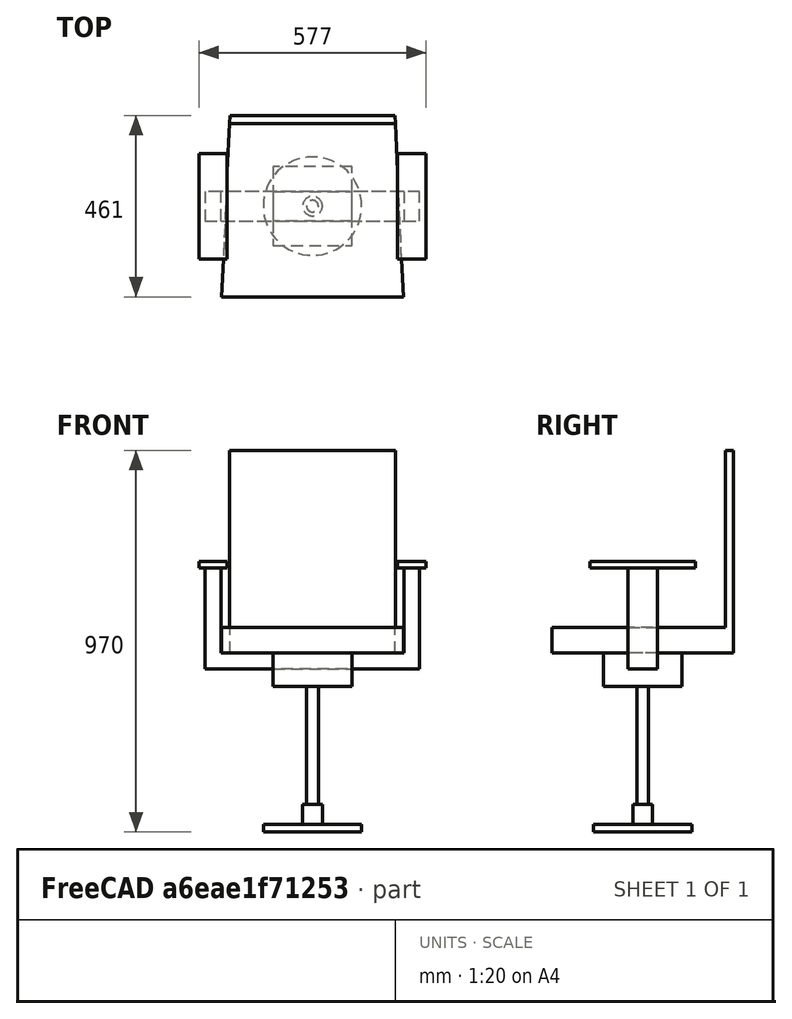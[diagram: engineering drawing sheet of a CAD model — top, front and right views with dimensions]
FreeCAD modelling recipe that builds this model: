
FCSTD DOCUMENT  (FreeCAD 1.0R39109 (Git))
Label: chair02_00502
License: All rights reserved
LicenseURL: https://en.wikipedia.org/wiki/All_rights_reserved
objects: Sketcher::SketchObject×10, PartDesign::Pad×10, TechDraw::DrawViewDimension×9, TechDraw::DrawViewAnnotation×9, PartDesign::Body×5, PartDesign::ShapeBinder×4, TechDraw::DrawSVGTemplate×3, TechDraw::DrawProjGroupItem×3, TechDraw::DrawPage×3, TechDraw::DrawViewSection×3, App::Part×1
note: 76 computed .brp shape members not serialized (recipe doc carries the construction recipe); baked Part::Feature solids carry a one-line shape summary decoded from their .brp

FEATURE [Sketcher::SketchObject] Sketch
  ArcFitTolerance = 1e-06
  AttachmentSupport = -> [XY_Plane]
  FullyConstrained = true
  MakeInternals = false
  MapMode = 5
  sketch-geometry (1):
    g0: Circle CenterX=0 CenterY=0 CenterZ=0 NormalX=0 NormalY=0 NormalZ=1 AngleXU=0 Radius=125
  constraints (2):
    c: Diameter(g0) = 250
    c: Coincident(g0,g-1)
FEATURE [PartDesign::Pad] Pad
  Direction = (0,0,1)
  Length = 20
  Length2 = 10
  Profile = -> Sketch
  ReferenceAxis = -> Sketch [N_Axis]
  Refine = true
  Suppressed = false
  Type = 0
FEATURE [Sketcher::SketchObject] Sketch001
  ArcFitTolerance = 1e-06
  AttachmentSupport = -> [Pad]
  FullyConstrained = true
  MakeInternals = false
  MapMode = 5
  Placement = pos=(0,0,20) rot=(0,0,1;0rad)
  sketch-geometry (1):
    g0: Circle CenterX=0 CenterY=0 CenterZ=0 NormalX=0 NormalY=0 NormalZ=1 AngleXU=0 Radius=25
  constraints (2):
    c: Diameter(g0) = 50
    c: Coincident(g0,g-1)
FEATURE [PartDesign::Pad] Pad001
  BaseFeature = -> Pad
  Direction = (0,0,1)
  Length = 50
  Length2 = 10
  Profile = -> Sketch001
  ReferenceAxis = -> Sketch001 [N_Axis]
  Refine = true
  Suppressed = false
  Type = 0
FEATURE [PartDesign::Body] Body  label="Body1"
  AllowCompound = false
  Group = -> [Sketch,Pad,Sketch001,Pad001]
  Origin = -> Origin
  Tip = -> Pad001
FEATURE [PartDesign::ShapeBinder] CopyPad001  label="Body2_Sketch_P.lane"
  Placement = pos=(0,0,50) rot=(0,0,1;0rad)
  TraceSupport = false
FEATURE [Sketcher::SketchObject] Sketch002
  ArcFitTolerance = 1e-06
  AttachmentSupport = -> [CopyPad001]
  FullyConstrained = true
  MakeInternals = false
  MapMode = 5
  Placement = pos=(0,0,70) rot=(0,0,1;0rad)
  sketch-geometry (1):
    g0: Circle CenterX=0 CenterY=0 CenterZ=0 NormalX=0 NormalY=0 NormalZ=1 AngleXU=0 Radius=15
  constraints (2):
    c: Diameter(g0) = 30
    c: Coincident(g0,g-1)
FEATURE [PartDesign::Pad] Pad002
  Direction = (0,0,1)
  Length = 300
  Length2 = 10
  Placement = pos=(0,0,50) rot=(0,0,1;0rad)
  Profile = -> Sketch002
  ReferenceAxis = -> Sketch002 [N_Axis]
  Refine = true
  Suppressed = false
  Type = 0
FEATURE [PartDesign::Body] Body001  label="Body2"
  AllowCompound = false
  Group = -> [CopyPad001,Sketch002,Pad002]
  Origin = -> Origin001
  Tip = -> Pad002
FEATURE [PartDesign::ShapeBinder] CopyPad002  label="Body3_Sketch_Plane"
  Placement = pos=(0,0,300) rot=(0,0,1;0rad)
  TraceSupport = false
FEATURE [Sketcher::SketchObject] Sketch003
  ArcFitTolerance = 1e-06
  AttachmentSupport = -> [CopyPad002]
  FullyConstrained = true
  MakeInternals = false
  MapMode = 5
  Placement = pos=(0,0,370) rot=(0,0,1;0rad)
  sketch-geometry (5):
    g0: LineSegment StartX=-100 StartY=-100 StartZ=0 EndX=100 EndY=-100 EndZ=0
    g1: LineSegment StartX=100 StartY=-100 StartZ=0 EndX=100 EndY=100 EndZ=0
    g2: LineSegment StartX=100 StartY=100 StartZ=0 EndX=-100 EndY=100 EndZ=0
    g3: LineSegment StartX=-100 StartY=100 StartZ=0 EndX=-100 EndY=-100 EndZ=0
    g4: GeomPoint [constr] X=0 Y=0 Z=0
  constraints (12):
    c: Coincident(g0,g1)
    c: Coincident(g1,g2)
    c: Coincident(g2,g3)
    c: Coincident(g3,g0)
    c: Horizontal(g0)
    c: Horizontal(g2)
    c: Vertical(g1)
    c: Vertical(g3)
    c: Symmetric(g2,g0,g4)
    c: Distance(g1,g3) = 200
    c: Distance(g0,g2) = 200
    c: Coincident(g4,g-1)
FEATURE [PartDesign::Pad] Pad003
  Direction = (0,0,1)
  Length = 45
  Length2 = 10
  Placement = pos=(0,0,300) rot=(0,0,1;0rad)
  Profile = -> Sketch003
  ReferenceAxis = -> Sketch003 [N_Axis]
  Refine = true
  Suppressed = false
  Type = 0
FEATURE [PartDesign::ShapeBinder] CopyPad003  label="Body4_Sketch_Plane"
  Placement = pos=(0,0,45) rot=(0,0,1;0rad)
  TraceSupport = false
FEATURE [Sketcher::SketchObject] Sketch004
  ArcFitTolerance = 1e-06
  AttachmentSupport = -> [CopyPad003]
  FullyConstrained = true
  MakeInternals = false
  MapMode = 5
  Placement = pos=(0,0,415) rot=(0,0,1;0rad)
  sketch-geometry (5):
    g0: LineSegment StartX=-272.5 StartY=-37.5 StartZ=0 EndX=272.5 EndY=-37.5 EndZ=0
    g1: LineSegment StartX=272.5 StartY=-37.5 StartZ=0 EndX=272.5 EndY=37.5 EndZ=0
    g2: LineSegment StartX=272.5 StartY=37.5 StartZ=0 EndX=-272.5 EndY=37.5 EndZ=0
    g3: LineSegment StartX=-272.5 StartY=37.5 StartZ=0 EndX=-272.5 EndY=-37.5 EndZ=0
    g4: GeomPoint [constr] X=0 Y=0 Z=0
  constraints (12):
    c: Coincident(g0,g1)
    c: Coincident(g1,g2)
    c: Coincident(g2,g3)
    c: Coincident(g3,g0)
    c: Horizontal(g0)
    c: Horizontal(g2)
    c: Vertical(g1)
    c: Vertical(g3)
    c: Symmetric(g2,g0,g4)
    c: Distance(g1,g3) = 545
    c: Distance(g0,g2) = 75
    c: Coincident(g4,g-1)
FEATURE [PartDesign::Pad] Pad004
  Direction = (0,0,1)
  Length = 40
  Length2 = 10
  Placement = pos=(0,0,45) rot=(0,0,1;0rad)
  Profile = -> Sketch004
  ReferenceAxis = -> Sketch004 [N_Axis]
  Refine = true
  Suppressed = false
  Type = 0
FEATURE [Sketcher::SketchObject] Sketch005
  ArcFitTolerance = 1e-06
  AttachmentSupport = -> [Pad004]
  ExternalGeometry = -> [Pad004]
  FullyConstrained = true
  MakeInternals = false
  MapMode = 5
  Placement = pos=(0,0,455) rot=(0,0,1;0rad)
  sketch-geometry (8):
    g0: LineSegment StartX=-272.5 StartY=37.5 StartZ=0 EndX=-272.5 EndY=-37.5 EndZ=0
    g1: LineSegment StartX=-272.5 StartY=-37.5 StartZ=0 EndX=-232.5 EndY=-37.5 EndZ=0
    g2: LineSegment StartX=-232.5 StartY=-37.5 StartZ=0 EndX=-232.5 EndY=37.5 EndZ=0
    g3: LineSegment StartX=-232.5 StartY=37.5 StartZ=0 EndX=-272.5 EndY=37.5 EndZ=0
    g4: LineSegment StartX=272.5 StartY=37.5 StartZ=0 EndX=232.5 EndY=37.5 EndZ=0
    g5: LineSegment StartX=232.5 StartY=37.5 StartZ=0 EndX=232.5 EndY=-37.5 EndZ=0
    g6: LineSegment StartX=232.5 StartY=-37.5 StartZ=0 EndX=272.5 EndY=-37.5 EndZ=0
    g7: LineSegment StartX=272.5 StartY=-37.5 StartZ=0 EndX=272.5 EndY=37.5 EndZ=0
  constraints (22):
    c: Coincident(g0,g1)
    c: Coincident(g1,g2)
    c: Coincident(g2,g3)
    c: Coincident(g3,g0)
    c: Vertical(g0)
    c: Vertical(g2)
    c: Horizontal(g1)
    c: Horizontal(g3)
    c: Coincident(g0,g-3)
    c: PointOnObject(g1,g-4)
    c: DistanceX(g3,g3) = 40
    c: Coincident(g4,g5)
    c: Coincident(g5,g6)
    c: Coincident(g6,g7)
    c: Coincident(g7,g4)
    c: Horizontal(g4)
    c: Horizontal(g6)
    c: Vertical(g5)
    c: Vertical(g7)
    c: Coincident(g4,g-3)
    c: PointOnObject(g5,g-4)
    c: Equal(g4,g3)
FEATURE [PartDesign::Pad] Pad005
  BaseFeature = -> Pad004
  Direction = (0,0,1)
  Length = 216
  Length2 = 10
  Placement = pos=(0,0,45) rot=(0,0,1;0rad)
  Profile = -> Sketch005
  ReferenceAxis = -> Sketch005 [N_Axis]
  Refine = true
  Suppressed = false
  Type = 0
FEATURE [Sketcher::SketchObject] Sketch006
  ArcFitTolerance = 1e-06
  AttachmentSupport = -> [Pad005]
  ExternalGeometry = -> [Pad005]
  FullyConstrained = true
  MakeInternals = false
  MapMode = 5
  Placement = pos=(0,0,671) rot=(0,0,1;0rad)
  sketch-geometry (16):
    g0: LineSegment StartX=-288.5 StartY=134 StartZ=0 EndX=-288.5 EndY=-134 EndZ=0
    g1: LineSegment StartX=-288.5 StartY=-134 StartZ=0 EndX=-216.5 EndY=-134 EndZ=0
    g2: LineSegment StartX=-216.5 StartY=-134 StartZ=0 EndX=-216.5 EndY=134 EndZ=0
    g3: LineSegment StartX=-216.5 StartY=134 StartZ=0 EndX=-288.5 EndY=134 EndZ=0
    g4: LineSegment StartX=216.5 StartY=134 StartZ=0 EndX=216.5 EndY=-134 EndZ=0
    g5: LineSegment StartX=216.5 StartY=-134 StartZ=0 EndX=288.5 EndY=-134 EndZ=0
    g6: LineSegment StartX=288.5 StartY=-134 StartZ=0 EndX=288.5 EndY=134 EndZ=0
    g7: LineSegment StartX=288.5 StartY=134 StartZ=0 EndX=216.5 EndY=134 EndZ=0
    g8: LineSegment [constr] StartX=-272.5 StartY=37.5 StartZ=0 EndX=-232.5 EndY=-37.5 EndZ=0
    g9: LineSegment [constr] StartX=-252.5 StartY=0 StartZ=0 EndX=-272.5 EndY=-37.5 EndZ=0
    g10: LineSegment [constr] StartX=232.5 StartY=37.5 StartZ=0 EndX=272.5 EndY=-37.5 EndZ=0
    g11: LineSegment [constr] StartX=272.5 StartY=37.5 StartZ=0 EndX=252.5 EndY=0 EndZ=0
    g12: LineSegment [constr] StartX=-216.5 StartY=134 StartZ=0 EndX=-288.5 EndY=-134 EndZ=0
    g13: LineSegment [constr] StartX=-288.5 StartY=134 StartZ=0 EndX=-252.5 EndY=0 EndZ=0
    g14: LineSegment [constr] StartX=216.5 StartY=134 StartZ=0 EndX=288.5 EndY=-134 EndZ=0
    g15: LineSegment [constr] StartX=288.5 StartY=134 StartZ=0 EndX=252.5 EndY=0 EndZ=0
  constraints (38):
    c: Coincident(g0,g1)
    c: Coincident(g1,g2)
    c: Coincident(g2,g3)
    c: Coincident(g3,g0)
    c: Vertical(g0)
    c: Vertical(g2)
    c: Horizontal(g1)
    c: Horizontal(g3)
    c: Coincident(g4,g5)
    c: Coincident(g5,g6)
    c: Coincident(g6,g7)
    c: Coincident(g7,g4)
    c: Vertical(g4)
    c: Vertical(g6)
    c: Horizontal(g5)
    c: Horizontal(g7)
    c: Equal(g7,g3)
    c: Equal(g2,g4)
    c: DistanceX(g3,g3) = 72
    c: Coincident(g8,g-4)
    c: Coincident(g8,g-3)
    c: Coincident(g9,g-4)
    c: Coincident(g10,g-5)
    c: Coincident(g10,g-6)
    c: Coincident(g11,g-6)
    c: Symmetric(g10,g10,g11)
    c: Symmetric(g8,g8,g9)
    c: Coincident(g12,g2)
    c: Coincident(g12,g0)
    c: Coincident(g13,g0)
    c: Symmetric(g12,g12,g13)
    c: Coincident(g9,g13)
    c: Coincident(g14,g4)
    c: Coincident(g14,g5)
    c: Coincident(g15,g6)
    c: Symmetric(g14,g14,g15)
    c: Coincident(g15,g11)
    c: DistanceY(g2,g2) = 268
FEATURE [PartDesign::Pad] Pad006
  BaseFeature = -> Pad005
  Direction = (0,0,1)
  Length = 17
  Length2 = 10
  Placement = pos=(0,0,45) rot=(0,0,1;0rad)
  Profile = -> Sketch006
  ReferenceAxis = -> Sketch006 [N_Axis]
  Refine = true
  Suppressed = false
  Type = 0
FEATURE [PartDesign::Body] Body003  label="Body4"
  AllowCompound = false
  Group = -> [CopyPad003,Sketch004,Pad004,Sketch005,Pad005,Sketch006,Pad006]
  Origin = -> Origin003
  Tip = -> Pad006
FEATURE [PartDesign::ShapeBinder] CopyPad006  label="Body5_Sketch_Plane"
  Placement = pos=(0,0,45) rot=(0,0,1;0rad)
  TraceSupport = false
FEATURE [Sketcher::SketchObject] Sketch009
  ArcFitTolerance = 1e-06
  AttachmentSupport = -> [Pad003]
  ExternalGeometry = -> [Pad003]
  FullyConstrained = true
  MakeInternals = false
  MapMode = 5
  Placement = pos=(0,0,415) rot=(0,0,1;0rad)
  sketch-geometry (8):
    g0: LineSegment StartX=-100 StartY=100 StartZ=0 EndX=-100 EndY=37.5 EndZ=0
    g1: LineSegment StartX=-100 StartY=37.5 StartZ=0 EndX=100 EndY=37.5 EndZ=0
    g2: LineSegment StartX=100 StartY=37.5 StartZ=0 EndX=100 EndY=100 EndZ=0
    g3: LineSegment StartX=100 StartY=100 StartZ=0 EndX=-100 EndY=100 EndZ=0
    g4: LineSegment StartX=100 StartY=-100 StartZ=0 EndX=100 EndY=-37.5 EndZ=0
    g5: LineSegment StartX=100 StartY=-37.5 StartZ=0 EndX=-100 EndY=-37.5 EndZ=0
    g6: LineSegment StartX=-100 StartY=-37.5 StartZ=0 EndX=-100 EndY=-100 EndZ=0
    g7: LineSegment StartX=-100 StartY=-100 StartZ=0 EndX=100 EndY=-100 EndZ=0
  constraints (21):
    c: Coincident(g0,g1)
    c: Coincident(g1,g2)
    c: Coincident(g2,g3)
    c: Coincident(g3,g0)
    c: Vertical(g0)
    c: Vertical(g2)
    c: Horizontal(g1)
    c: Horizontal(g3)
    c: Coincident(g0,g-3)
    c: PointOnObject(g1,g-4)
    c: Coincident(g4,g5)
    c: Coincident(g5,g6)
    c: Coincident(g6,g7)
    c: Coincident(g7,g4)
    c: Vertical(g6)
    c: Horizontal(g5)
    c: Horizontal(g7)
    c: Coincident(g4,g-4)
    c: PointOnObject(g5,g-3)
    c: DistanceY(g4,g1) = 75
    c: Symmetric(g1,g4,g-1)
FEATURE [PartDesign::Pad] Pad009
  BaseFeature = -> Pad003
  Direction = (0,0,1)
  Length = 40
  Length2 = 10
  Placement = pos=(0,0,300) rot=(0,0,1;0rad)
  Profile = -> Sketch009
  ReferenceAxis = -> Sketch009 [N_Axis]
  Refine = true
  Suppressed = false
  Type = 0
FEATURE [PartDesign::Body] Body002  label="Body3"
  AllowCompound = false
  Group = -> [CopyPad002,Sketch003,Pad003,Sketch009,Pad009]
  Origin = -> Origin002
  Tip = -> Pad009
FEATURE [Sketcher::SketchObject] Sketch007
  ArcFitTolerance = 1e-06
  AttachmentSupport = -> [CopyPad006]
  FullyConstrained = true
  MakeInternals = false
  MapMode = 5
  Placement = pos=(0,0,455) rot=(0,0,1;0rad)
  sketch-geometry (8):
    g0: LineSegment StartX=-210 StartY=230.5 StartZ=0 EndX=-231 EndY=-230.5 EndZ=0
    g1: LineSegment StartX=-231 StartY=-230.5 StartZ=0 EndX=231 EndY=-230.5 EndZ=0
    g2: LineSegment StartX=231 StartY=-230.5 StartZ=0 EndX=210 EndY=230.5 EndZ=0
    g3: LineSegment StartX=210 StartY=230.5 StartZ=0 EndX=-210 EndY=230.5 EndZ=0
    g4: LineSegment [constr] StartX=210 StartY=230.5 StartZ=0 EndX=2.84e-14 EndY=0 EndZ=0
    g5: LineSegment [constr] StartX=2.84e-14 StartY=0 StartZ=0 EndX=-210 EndY=230.5 EndZ=0
    g6: LineSegment [constr] StartX=210 StartY=230.5 StartZ=0 EndX=210 EndY=0 EndZ=0
    g7: LineSegment [constr] StartX=231 StartY=-230.5 StartZ=0 EndX=231 EndY=0 EndZ=0
  constraints (20):
    c: Coincident(g2,g1)
    c: DistanceX(g1,g1) = 462
    c: DistanceX(g3,g3) = 420
    c: Coincident(g1,g0)
    c: Symmetric(g2,g0,g-2)
    c: Coincident(g2,g3)
    c: Coincident(g3,g0)
    c: Coincident(g4,g2)
    c: Coincident(g4,g-1)
    c: Coincident(g5,g4)
    c: Coincident(g5,g0)
    c: DistanceY(g2,g2) = 461
    c: Coincident(g6,g2)
    c: PointOnObject(g6,g-1)
    c: Vertical(g6)
    c: Coincident(g7,g1)
    c: PointOnObject(g7,g-1)
    c: Vertical(g7)
    c: Equal(g7,g6)
    c: Symmetric(g1,g0,g-2)
FEATURE [PartDesign::Pad] Pad007
  Direction = (0,0,1)
  Length = 65
  Length2 = 10
  Placement = pos=(0,0,45) rot=(0,0,1;0rad)
  Profile = -> Sketch007
  ReferenceAxis = -> Sketch007 [N_Axis]
  Refine = true
  Suppressed = false
  Type = 0
FEATURE [Sketcher::SketchObject] Sketch008
  ArcFitTolerance = 1e-06
  AttachmentSupport = -> [Pad007]
  ExternalGeometry = -> [Pad007]
  FullyConstrained = true
  MakeInternals = false
  MapMode = 5
  Placement = pos=(0,0,520) rot=(0,0,1;0rad)
  sketch-geometry (4):
    g0: LineSegment StartX=-210 StartY=230.5 StartZ=0 EndX=210 EndY=230.5 EndZ=0
    g1: LineSegment StartX=-210 StartY=230.5 StartZ=0 EndX=-210.957 EndY=209.5 EndZ=0
    g2: LineSegment StartX=-210.957 StartY=209.5 StartZ=0 EndX=210.957 EndY=209.5 EndZ=0
    g3: LineSegment StartX=210 StartY=230.5 StartZ=0 EndX=210.957 EndY=209.5 EndZ=0
  constraints (10):
    c: Coincident(g0,g-3)
    c: Coincident(g0,g-4)
    c: Coincident(g1,g0)
    c: PointOnObject(g1,g-3)
    c: Coincident(g2,g1)
    c: PointOnObject(g2,g-4)
    c: Horizontal(g2)
    c: Coincident(g3,g0)
    c: Coincident(g3,g2)
    c: DistanceY(g1,g1) = 21
FEATURE [PartDesign::Pad] Pad008
  BaseFeature = -> Pad007
  Direction = (0,0,1)
  Length = 450
  Length2 = 10
  Placement = pos=(0,0,45) rot=(0,0,1;0rad)
  Profile = -> Sketch008
  ReferenceAxis = -> Sketch008 [N_Axis]
  Refine = true
  Suppressed = false
  Type = 0
FEATURE [PartDesign::Body] Body004  label="Body5"
  AllowCompound = false
  Group = -> [CopyPad006,Sketch007,Pad007,Sketch008,Pad008]
  Origin = -> Origin004
  Tip = -> Pad008
FEATURE [App::Part] Part  label="chair02"
  Group = -> [Body,Body001,Body002,Body003,Body004]
  Origin = -> Origin005
FEATURE [TechDraw::DrawSVGTemplate] Template  label="テンプレート"
  Height = 210
  Orientation = 1
  Template = <userpath>/AppData/Local/Programs/FreeCAD 1.0/data/Mod/TechDraw/Templates/A4_Landscape_blank.svg
  Width = 297
FEATURE [TechDraw::DrawProjGroupItem] View
  CoarseView = false
  Direction = (0,0,1)
  Focus = 100
  HardHidden = true
  IsoCount = 0
  IsoHidden = false
  IsoVisible = false
  LockPosition = false
  Perspective = false
  Rotation = 0
  RotationVector = (1,0,0)
  Scale = 0.333333
  ScaleType = 2
  ScrubCount = 1
  SeamHidden = false
  SeamVisible = false
  SmoothHidden = false
  SmoothVisible = true
  Source = -> [Part]
  Type = 0
  X = 131.425
  XDirection = (1,0,0)
  Y = 107.897
FEATURE [TechDraw::DrawViewDimension] Dimension  label="寸法"
  AngleOverride = false
  Arbitrary = false
  ArbitraryTolerances = false
  BoxCorners = (2) [(-96.1666,-76.8333,0),(96.1666,76.8333,0)]
  EqualTolerance = true
  ExtensionAngle = 0
  FormatSpec = %.2w
  FormatSpecOverTolerance = %+.2w
  FormatSpecUnderTolerance = %+.2w
  Inverted = false
  LineAngle = 0
  LockPosition = false
  MeasureType = 1
  OverTolerance = 0
  References2D = -> [View]
  Rotation = 0
  Scale = 0.2
  ScaleType = 2
  TheoreticalExact = false
  Type = 1
  UnderTolerance = 0
  X = 0
  Y = 93.9298
FEATURE [TechDraw::DrawViewDimension] Dimension001  label="寸法001"
  AngleOverride = false
  Arbitrary = false
  ArbitraryTolerances = false
  BoxCorners = (2) [(-96.1666,-76.8333,0),(96.1666,76.8333,0)]
  EqualTolerance = true
  ExtensionAngle = 0
  FormatSpec = %.2w
  FormatSpecOverTolerance = %+.2w
  FormatSpecUnderTolerance = %+.2w
  Inverted = false
  LineAngle = 0
  LockPosition = false
  MeasureType = 1
  OverTolerance = 0
  References2D = -> [View]
  Rotation = 0
  Scale = 0.2
  ScaleType = 2
  TheoreticalExact = false
  Type = 2
  UnderTolerance = 0
  X = 135.701
  Y = 0
FEATURE [TechDraw::DrawViewDimension] Dimension002  label="寸法002"
  AngleOverride = false
  Arbitrary = false
  ArbitraryTolerances = false
  BoxCorners = (2) [(-96.1666,-76.8333,0),(96.1666,76.8333,0)]
  EqualTolerance = true
  ExtensionAngle = 0
  FormatSpec = %.2w
  FormatSpecOverTolerance = %+.2w
  FormatSpecUnderTolerance = %+.2w
  Inverted = false
  LineAngle = 0
  LockPosition = false
  MeasureType = 1
  OverTolerance = 0
  References2D = -> [View]
  Rotation = 0
  Scale = 0.2
  ScaleType = 2
  TheoreticalExact = false
  Type = 2
  UnderTolerance = 0
  X = 113.57
  Y = 61.6706
FEATURE [TechDraw::DrawViewDimension] Dimension003  label="寸法003"
  AngleOverride = false
  Arbitrary = false
  ArbitraryTolerances = false
  BoxCorners = (2) [(-96.1666,-76.8333,0),(96.1666,76.8333,0)]
  EqualTolerance = true
  ExtensionAngle = 0
  FormatSpec = %.2w
  FormatSpecOverTolerance = %+.2w
  FormatSpecUnderTolerance = %+.2w
  Inverted = false
  LineAngle = 0
  LockPosition = false
  MeasureType = 1
  OverTolerance = 0
  References2D = -> [View]
  Rotation = 0
  Scale = 0.2
  ScaleType = 2
  TheoreticalExact = false
  Type = 2
  UnderTolerance = 0
  X = 125.233
  Y = 0.063601
FEATURE [TechDraw::DrawViewDimension] Dimension004  label="寸法004"
  AngleOverride = false
  Arbitrary = false
  ArbitraryTolerances = false
  BoxCorners = (2) [(-96.1666,-76.8333,0),(96.1666,76.8333,0)]
  EqualTolerance = true
  ExtensionAngle = 0
  FormatSpec = %.2w
  FormatSpecOverTolerance = %+.2w
  FormatSpecUnderTolerance = %+.2w
  Inverted = false
  LineAngle = 0
  LockPosition = false
  MeasureType = 1
  OverTolerance = 0
  References2D = -> [View]
  Rotation = 0
  Scale = 0.2
  ScaleType = 2
  TheoreticalExact = false
  Type = 1
  UnderTolerance = 0
  X = -84.1666
  Y = 58.5053
FEATURE [TechDraw::DrawViewDimension] Dimension005  label="寸法005"
  AngleOverride = false
  Arbitrary = false
  ArbitraryTolerances = false
  BoxCorners = (2) [(-96.1666,-76.8333,0),(96.1666,76.8333,0)]
  EqualTolerance = true
  ExtensionAngle = 0
  FormatSpec = %.2w
  FormatSpecOverTolerance = %+.2w
  FormatSpecUnderTolerance = %+.2w
  Inverted = false
  LineAngle = 0
  LockPosition = false
  MeasureType = 1
  OverTolerance = 0
  References2D = -> [View]
  Rotation = 0
  Scale = 0.2
  ScaleType = 2
  TheoreticalExact = false
  Type = 2
  UnderTolerance = 0
  X = -108.801
  Y = 0
FEATURE [TechDraw::DrawViewDimension] Dimension006  label="寸法006"
  AngleOverride = false
  Arbitrary = false
  ArbitraryTolerances = false
  BoxCorners = (2) [(-96.1666,-76.8333,0),(96.1666,76.8333,0)]
  EqualTolerance = true
  ExtensionAngle = 0
  FormatSpec = %.2w
  FormatSpecOverTolerance = %+.2w
  FormatSpecUnderTolerance = %+.2w
  Inverted = false
  LineAngle = 0
  LockPosition = false
  MeasureType = 1
  OverTolerance = 0
  References2D = -> [View]
  Rotation = 0
  Scale = 0.2
  ScaleType = 2
  TheoreticalExact = false
  Type = 1
  UnderTolerance = 0
  X = 0
  Y = -83.8244
FEATURE [TechDraw::DrawPage] Page  label="用紙"
  KeepUpdated = true
  NextBalloonIndex = 1
  ProjectionType = 0
  Template = -> Template
  Views = -> [View,Dimension,Dimension001,Dimension002,Dimension003,Dimension004,Dimension005,Dimension006]
FEATURE [TechDraw::DrawSVGTemplate] Template001  label="テンプレート001"
  Height = 210
  Orientation = 1
  Template = <userpath>/AppData/Local/Programs/FreeCAD 1.0/data/Mod/TechDraw/Templates/A4_Landscape_blank.svg
  Width = 297
FEATURE [TechDraw::DrawSVGTemplate] Template002  label="テンプレート002"
  Height = 210
  Orientation = 1
  Template = <userpath>/AppData/Local/Programs/FreeCAD 1.0/data/Mod/TechDraw/Templates/A4_Landscape_blank.svg
  Width = 297
FEATURE [TechDraw::DrawProjGroupItem] View001
  CoarseView = false
  Direction = (0,-1,0)
  Focus = 100
  HardHidden = true
  IsoCount = 0
  IsoHidden = false
  IsoVisible = false
  LockPosition = false
  Perspective = false
  Rotation = 0
  RotationVector = (1,0,0)
  Scale = 0.2
  ScaleType = 2
  ScrubCount = 1
  SeamHidden = false
  SeamVisible = false
  SmoothHidden = false
  SmoothVisible = true
  Source = -> [Part]
  Type = 0
  X = 72.2264
  XDirection = (1,0,0)
  Y = 108.632
FEATURE [TechDraw::DrawViewSection] SectionView  label="セクション  - "
  BaseView = -> View001
  CoarseView = false
  CutSurfaceDisplay = 2
  Direction = (1e-16,0,1)
  FileGeomPattern = <userpath>\AppData\Local\Programs\FreeCAD 1.0\data\Mod/TechDraw/PAT/FCPAT.pat
  FileHatchPattern = <userpath>\AppData\Local\Programs\FreeCAD 1.0\data\Mod/TechDraw/Patterns/simple.svg
  Focus = 100
  FuseBeforeCut = false
  HardHidden = true
  HatchOffset = (0,0,0)
  HatchRotation = 0
  HatchScale = 1
  IsoCount = 0
  IsoHidden = false
  IsoVisible = false
  LockPosition = false
  NameGeomPattern = Diamond
  Perspective = false
  Rotation = 0
  Scale = 0.15
  ScaleType = 2
  ScrubCount = 1
  SeamHidden = false
  SeamVisible = false
  SectionDirection = 4
  SectionLineStretch = 1
  SectionNormal = (1e-16,0,1)
  SectionOrigin = (0,0,581)
  SmoothHidden = false
  SmoothVisible = true
  Source = -> [Part]
  TrimAfterCut = false
  UsePreviousCut = false
  X = 215.858
  XDirection = (1,0,-1e-16)
  Y = 166.085
FEATURE [TechDraw::DrawViewSection] SectionView001  label="セクション001  - "
  BaseView = -> View001
  CoarseView = false
  CutSurfaceDisplay = 2
  Direction = (1e-16,0,1)
  FileGeomPattern = <userpath>\AppData\Local\Programs\FreeCAD 1.0\data\Mod/TechDraw/PAT/FCPAT.pat
  FileHatchPattern = <userpath>\AppData\Local\Programs\FreeCAD 1.0\data\Mod/TechDraw/Patterns/simple.svg
  Focus = 100
  FuseBeforeCut = false
  HardHidden = true
  HatchOffset = (0,0,0)
  HatchRotation = 0
  HatchScale = 1
  IsoCount = 0
  IsoHidden = false
  IsoVisible = false
  LockPosition = false
  NameGeomPattern = Diamond
  Perspective = false
  Rotation = 0
  Scale = 0.15
  ScaleType = 2
  ScrubCount = 1
  SeamHidden = false
  SeamVisible = false
  SectionDirection = 4
  SectionLineStretch = 1
  SectionNormal = (1e-16,0,1)
  SectionOrigin = (0,0,437)
  SmoothHidden = false
  SmoothVisible = true
  Source = -> [Part]
  TrimAfterCut = false
  UsePreviousCut = false
  X = 215.086
  XDirection = (1,0,-1e-16)
  Y = 92.3168
FEATURE [TechDraw::DrawViewSection] SectionView002  label="セクション002  - "
  BaseView = -> View001
  CoarseView = false
  CutSurfaceDisplay = 2
  Direction = (1e-16,0,1)
  FileGeomPattern = <userpath>\AppData\Local\Programs\FreeCAD 1.0\data\Mod/TechDraw/PAT/FCPAT.pat
  FileHatchPattern = <userpath>\AppData\Local\Programs\FreeCAD 1.0\data\Mod/TechDraw/Patterns/simple.svg
  Focus = 100
  FuseBeforeCut = false
  HardHidden = true
  HatchOffset = (0,0,0)
  HatchRotation = 0
  HatchScale = 1
  IsoCount = 0
  IsoHidden = false
  IsoVisible = false
  LockPosition = false
  NameGeomPattern = Diamond
  Perspective = false
  Rotation = 0
  Scale = 0.15
  ScaleType = 2
  ScrubCount = 1
  SeamHidden = false
  SeamVisible = false
  SectionDirection = 4
  SectionLineStretch = 1
  SectionNormal = (1e-16,0,1)
  SectionOrigin = (0,0,200)
  SmoothHidden = false
  SmoothVisible = true
  Source = -> [Part]
  TrimAfterCut = false
  UsePreviousCut = false
  X = 214.868
  XDirection = (1,0,-1e-16)
  Y = 24.434
FEATURE [TechDraw::DrawViewDimension] Dimension013  label="寸法013"
  AngleOverride = false
  Arbitrary = false
  ArbitraryTolerances = false
  BoxCorners = (2) [(-18.75,-18.75,0),(18.75,18.75,0)]
  EqualTolerance = true
  ExtensionAngle = 0
  FormatSpec = ⌀%.2w
  FormatSpecOverTolerance = %+.2w
  FormatSpecUnderTolerance = %+.2w
  Inverted = false
  LineAngle = 0
  LockPosition = false
  MeasureType = 1
  OverTolerance = 0
  References2D = -> [SectionView002]
  Rotation = 0
  Scale = 0.2
  ScaleType = 2
  TheoreticalExact = false
  Type = 5
  UnderTolerance = 0
  X = 9.91703
  Y = -6.83959
FEATURE [TechDraw::DrawViewAnnotation] Annotation  label="注釈"
  Font = osifont
  LineSpace = 100
  LockPosition = false
  MaxWidth = -1
  Rotation = 0
  Scale = 0.2
  ScaleType = 2
  Text = A
  TextSize = 5
  TextStyle = 0
  X = 143.937
  Y = 118.99
FEATURE [TechDraw::DrawViewAnnotation] Annotation001  label="注釈001"
  Font = osifont
  LineSpace = 100
  LockPosition = false
  MaxWidth = -1
  Rotation = 0
  Scale = 0.2
  ScaleType = 2
  Text = A
  TextSize = 5
  TextStyle = 0
  X = 9.25009
  Y = 118.99
FEATURE [TechDraw::DrawViewAnnotation] Annotation002  label="注釈002"
  Font = osifont
  LineSpace = 100
  LockPosition = false
  MaxWidth = -1
  Rotation = 0
  Scale = 0.2
  ScaleType = 2
  Text = B
  TextSize = 5
  TextStyle = 0
  X = 9.25009
  Y = 89.4351
FEATURE [TechDraw::DrawViewAnnotation] Annotation003  label="注釈003"
  Font = osifont
  LineSpace = 100
  LockPosition = false
  MaxWidth = -1
  Rotation = 0
  Scale = 0.2
  ScaleType = 2
  Text = B
  TextSize = 5
  TextStyle = 0
  X = 145.458
  Y = 89.4351
FEATURE [TechDraw::DrawViewAnnotation] Annotation004  label="注釈004"
  Font = osifont
  LineSpace = 100
  LockPosition = false
  MaxWidth = -1
  Rotation = 0
  Scale = 0.2
  ScaleType = 2
  Text = C
  TextSize = 5
  TextStyle = 0
  X = 145.458
  Y = 40.7495
FEATURE [TechDraw::DrawViewAnnotation] Annotation005  label="注釈005"
  Font = osifont
  LineSpace = 100
  LockPosition = false
  MaxWidth = -1
  Rotation = 0
  Scale = 0.2
  ScaleType = 2
  Text = C
  TextSize = 5
  TextStyle = 0
  X = 9.25009
  Y = 43.6474
FEATURE [TechDraw::DrawViewAnnotation] Annotation006  label="注釈006"
  Font = osifont
  LineSpace = 100
  LockPosition = false
  MaxWidth = -1
  Rotation = 0
  Scale = 0.2
  ScaleType = 2
  Text = A-A
  TextSize = 5
  TextStyle = 0
  X = 215.858
  Y = 205.891
FEATURE [TechDraw::DrawViewAnnotation] Annotation007  label="注釈007"
  Font = osifont
  LineSpace = 100
  LockPosition = false
  MaxWidth = -1
  Rotation = 0
  Scale = 0.2
  ScaleType = 2
  Text = B-B
  TextSize = 5
  TextStyle = 0
  X = 215.858
  Y = 117.871
FEATURE [TechDraw::DrawViewAnnotation] Annotation008  label="注釈008"
  Font = osifont
  LineSpace = 100
  LockPosition = false
  MaxWidth = -1
  Rotation = 0
  Scale = 0.2
  ScaleType = 2
  Text = C -C
  TextSize = 5
  TextStyle = 0
  X = 215.858
  Y = 48.4539
FEATURE [TechDraw::DrawPage] Page002  label="用紙002"
  KeepUpdated = true
  NextBalloonIndex = 1
  ProjectionType = 0
  Template = -> Template002
  Views = -> [View001,SectionView,SectionView001,SectionView002,Dimension013,Annotation,Annotation001,Annotation002,Annotation003,Annotation004,Annotation005,Annotation006,Annotation007,Annotation008]
FEATURE [TechDraw::DrawProjGroupItem] View002
  CoarseView = false
  Direction = (0,-1,0)
  Focus = 100
  HardHidden = true
  IsoCount = 0
  IsoHidden = false
  IsoVisible = false
  LockPosition = false
  Perspective = false
  Rotation = 0
  RotationVector = (1,0,0)
  Scale = 0.2
  ScaleType = 2
  ScrubCount = 1
  SeamHidden = false
  SeamVisible = false
  SmoothHidden = false
  SmoothVisible = true
  Source = -> [Part]
  Type = 0
  X = 144.274
  XDirection = (1,0,0)
  Y = 104.736
FEATURE [TechDraw::DrawViewDimension] Dimension022  label="寸法022"
  AngleOverride = false
  Arbitrary = false
  ArbitraryTolerances = false
  BoxCorners = (2) [(-48.0834,-80.8335,-1e-07),(48.0834,80.8335,1e-07)]
  EqualTolerance = true
  ExtensionAngle = 0
  FormatSpec = %.2w
  FormatSpecOverTolerance = %+.2w
  FormatSpecUnderTolerance = %+.2w
  Inverted = false
  LineAngle = 0
  LockPosition = false
  MeasureType = 1
  OverTolerance = 0
  References2D = -> [View002]
  Rotation = 0
  Scale = 0.2
  ScaleType = 2
  TheoreticalExact = false
  Type = 2
  UnderTolerance = 0
  X = 44.6521
  Y = -44.1668
FEATURE [TechDraw::DrawPage] Page001  label="用紙001"
  KeepUpdated = true
  NextBalloonIndex = 1
  ProjectionType = 0
  Template = -> Template001
  Views = -> [View002,Dimension022]
